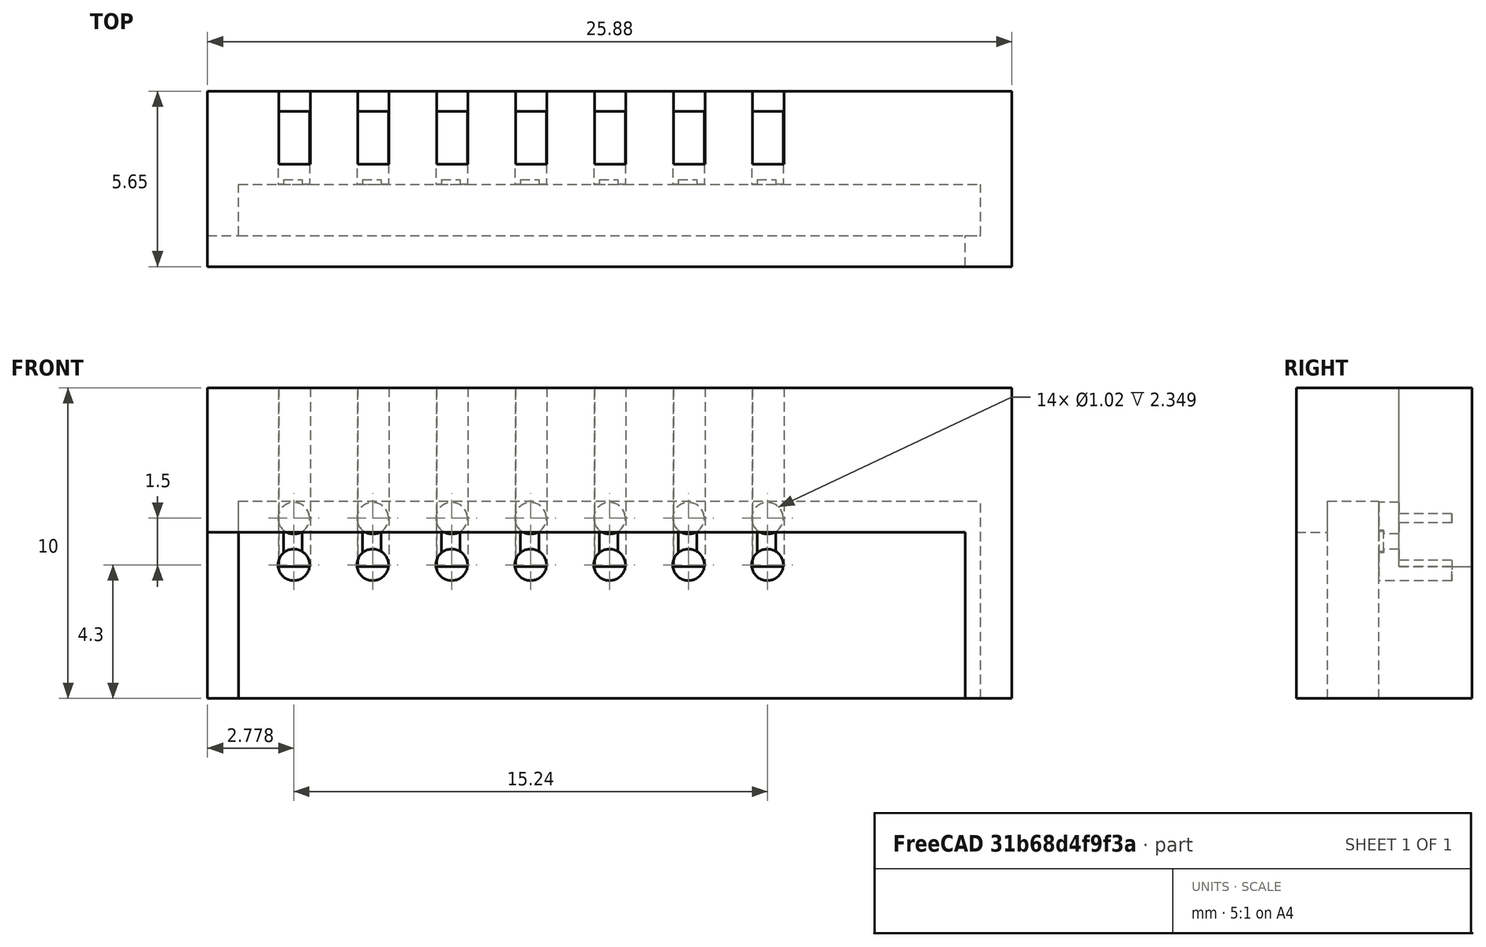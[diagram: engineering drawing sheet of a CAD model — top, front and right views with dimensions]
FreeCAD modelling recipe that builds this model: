
FCSTD DOCUMENT  (FreeCAD 0.16R6712 (Git))
Label: OBI-Socket-PrgConnector-v2
License: All rights reserved
LicenseURL: http://en.wikipedia.org/wiki/All_rights_reserved
objects: Part::Box×17, Part::Cylinder×14, Part::MultiFuse×10, Part::Cut×3, Part::Feature×1
note: 45 computed .brp shape members not serialized (recipe doc carries the construction recipe); baked Part::Feature solids carry a one-line shape summary decoded from their .brp

FEATURE [Part::Box] Box  label="Würfel"
  Height = 6.35
  Length = 23.876
  Placement = pos=(1,1,0) rot=(0,0,1;0rad)
  Width = 1.651
FEATURE [Part::Box] Box001  label="Würfel001"
  Height = 10
  Length = 25.876
  Width = 5.651
FEATURE [Part::Box] Box002  label="Würfel002"
  Height = 5.35
  Length = 24.376
  Placement = pos=(0,-2,0) rot=(0,0,1;0rad)
  Width = 3
FEATURE [Part::MultiFuse] Fusion
  Shapes = -> [Box,Box002]
FEATURE [Part::Cut] Cut
  Base = -> Box001
  Tool = -> Fusion
FEATURE [Part::Cylinder] Cylinder  label="Zylinder"
  Angle = 360
  Height = 3
  Placement = pos=(2.778,5,5.8) rot=(1,0,0;1.5708rad)
  Radius = 0.508
FEATURE [Part::Cylinder] Cylinder001  label="Zylinder001"
  Angle = 360
  Height = 3
  Placement = pos=(2.778,5,4.3) rot=(1,0,0;1.5708rad)
  Radius = 0.508
FEATURE [Part::Box] Box003  label="Würfel003"
  Height = 6
  Length = 1.016
  Placement = pos=(2.29,3.3,4.25) rot=(0,0,1;0rad)
  Width = 3
FEATURE [Part::MultiFuse] Fusion001
  Shapes = -> [Cylinder,Box003,Cylinder001]
FEATURE [Part::Cylinder] Cylinder002  label="Zylinder002"
  Angle = 360
  Height = 3
  Placement = pos=(2.778,5,5.8) rot=(1,0,0;1.5708rad)
  Radius = 0.508
FEATURE [Part::Cylinder] Cylinder003  label="Zylinder003"
  Angle = 360
  Height = 3
  Placement = pos=(2.778,5,4.3) rot=(1,0,0;1.5708rad)
  Radius = 0.508
FEATURE [Part::Box] Box004  label="Würfel004"
  Height = 6
  Length = 1.016
  Placement = pos=(2.29,3.3,4.25) rot=(0,0,1;0rad)
  Width = 3
FEATURE [Part::MultiFuse] Fusion002
  Placement = pos=(2.54,0,0) rot=(0,0,1;0rad)
  Shapes = -> [Cylinder002,Box004,Cylinder003]
FEATURE [Part::Cylinder] Cylinder004  label="Zylinder004"
  Angle = 360
  Height = 3
  Placement = pos=(2.778,5,5.8) rot=(1,0,0;1.5708rad)
  Radius = 0.508
FEATURE [Part::Cylinder] Cylinder005  label="Zylinder005"
  Angle = 360
  Height = 3
  Placement = pos=(2.778,5,4.3) rot=(1,0,0;1.5708rad)
  Radius = 0.508
FEATURE [Part::Box] Box005  label="Würfel005"
  Height = 6
  Length = 1.016
  Placement = pos=(2.29,3.3,4.25) rot=(0,0,1;0rad)
  Width = 3
FEATURE [Part::MultiFuse] Fusion003
  Placement = pos=(5.08,0,0) rot=(0,0,1;0rad)
  Shapes = -> [Cylinder004,Box005,Cylinder005]
FEATURE [Part::Cylinder] Cylinder006  label="Zylinder006"
  Angle = 360
  Height = 3
  Placement = pos=(2.778,5,5.8) rot=(1,0,0;1.5708rad)
  Radius = 0.508
FEATURE [Part::Cylinder] Cylinder007  label="Zylinder007"
  Angle = 360
  Height = 3
  Placement = pos=(2.778,5,4.3) rot=(1,0,0;1.5708rad)
  Radius = 0.508
FEATURE [Part::Box] Box006  label="Würfel006"
  Height = 6
  Length = 1.016
  Placement = pos=(2.29,3.3,4.25) rot=(0,0,1;0rad)
  Width = 3
FEATURE [Part::MultiFuse] Fusion004
  Placement = pos=(7.62,0,0) rot=(0,0,1;0rad)
  Shapes = -> [Cylinder006,Box006,Cylinder007]
FEATURE [Part::Cylinder] Cylinder008  label="Zylinder008"
  Angle = 360
  Height = 3
  Placement = pos=(2.778,5,5.8) rot=(1,0,0;1.5708rad)
  Radius = 0.508
FEATURE [Part::Cylinder] Cylinder009  label="Zylinder009"
  Angle = 360
  Height = 3
  Placement = pos=(2.778,5,4.3) rot=(1,0,0;1.5708rad)
  Radius = 0.508
FEATURE [Part::Box] Box007  label="Würfel007"
  Height = 6
  Length = 1.016
  Placement = pos=(2.29,3.3,4.25) rot=(0,0,1;0rad)
  Width = 3
FEATURE [Part::MultiFuse] Fusion005
  Placement = pos=(10.16,0,0) rot=(0,0,1;0rad)
  Shapes = -> [Cylinder008,Box007,Cylinder009]
FEATURE [Part::Cylinder] Cylinder010  label="Zylinder010"
  Angle = 360
  Height = 3
  Placement = pos=(2.778,5,5.8) rot=(1,0,0;1.5708rad)
  Radius = 0.508
FEATURE [Part::Cylinder] Cylinder011  label="Zylinder011"
  Angle = 360
  Height = 3
  Placement = pos=(2.778,5,4.3) rot=(1,0,0;1.5708rad)
  Radius = 0.508
FEATURE [Part::Box] Box008  label="Würfel008"
  Height = 6
  Length = 1.016
  Placement = pos=(2.29,3.3,4.25) rot=(0,0,1;0rad)
  Width = 3
FEATURE [Part::MultiFuse] Fusion006
  Placement = pos=(12.7,0,0) rot=(0,0,1;0rad)
  Shapes = -> [Cylinder010,Box008,Cylinder011]
FEATURE [Part::Cylinder] Cylinder012  label="Zylinder012"
  Angle = 360
  Height = 3
  Placement = pos=(2.778,5,5.8) rot=(1,0,0;1.5708rad)
  Radius = 0.508
FEATURE [Part::Cylinder] Cylinder013  label="Zylinder013"
  Angle = 360
  Height = 3
  Placement = pos=(2.778,5,4.3) rot=(1,0,0;1.5708rad)
  Radius = 0.508
FEATURE [Part::Box] Box009  label="Würfel009"
  Height = 6
  Length = 1.016
  Placement = pos=(2.29,3.3,4.25) rot=(0,0,1;0rad)
  Width = 3
FEATURE [Part::MultiFuse] Fusion007
  Placement = pos=(15.24,0,0) rot=(0,0,1;0rad)
  Shapes = -> [Cylinder012,Box009,Cylinder013]
FEATURE [Part::MultiFuse] Fusion008
  Shapes = -> [Fusion001,Fusion004,Fusion003,Fusion005,Fusion007,Fusion002,Fusion006]
FEATURE [Part::Cut] Cut001
  Base = -> Cut
  Tool = -> Fusion008
FEATURE [Part::Box] Box010  label="Würfel010"
  Height = 1
  Length = 0.6
  Placement = pos=(2.45,1.9,4.5) rot=(0,0,1;0rad)
  Width = 1
FEATURE [Part::Box] Box011  label="Würfel011"
  Height = 1
  Length = 0.6
  Placement = pos=(4.9911,1.9,4.5) rot=(0,0,1;0rad)
  Width = 1
FEATURE [Part::Box] Box012  label="Würfel012"
  Height = 1
  Length = 0.6
  Placement = pos=(7.5311,1.9,4.5) rot=(0,0,1;0rad)
  Width = 1
FEATURE [Part::Box] Box013  label="Würfel013"
  Height = 1
  Length = 0.6
  Placement = pos=(10.0711,1.9,4.5) rot=(0,0,1;0rad)
  Width = 1
FEATURE [Part::Box] Box014  label="Würfel014"
  Height = 1
  Length = 0.6
  Placement = pos=(12.6111,1.9,4.5) rot=(0,0,1;0rad)
  Width = 1
FEATURE [Part::Box] Box015  label="Würfel015"
  Height = 1
  Length = 0.6
  Placement = pos=(15.1511,1.9,4.5) rot=(0,0,1;0rad)
  Width = 1
FEATURE [Part::Box] Box016  label="Würfel016"
  Height = 1
  Length = 0.6
  Placement = pos=(17.6911,1.9,4.5) rot=(0,0,1;0rad)
  Width = 1
FEATURE [Part::MultiFuse] Fusion009
  Placement = pos=(0,-0.1,0) rot=(0,0,1;0rad)
  Shapes = -> [Box010,Box011,Box015,Box016,Box012,Box013,Box014]
FEATURE [Part::Cut] Cut002
  Base = -> Cut001
  Tool = -> Fusion009
FEATURE [Part::Feature] Cut002_solid001  label="Cut002 (Solid)001"
  shape: bbox 25.88 x 5.651 x 10 mm, 91 faces (baked)
